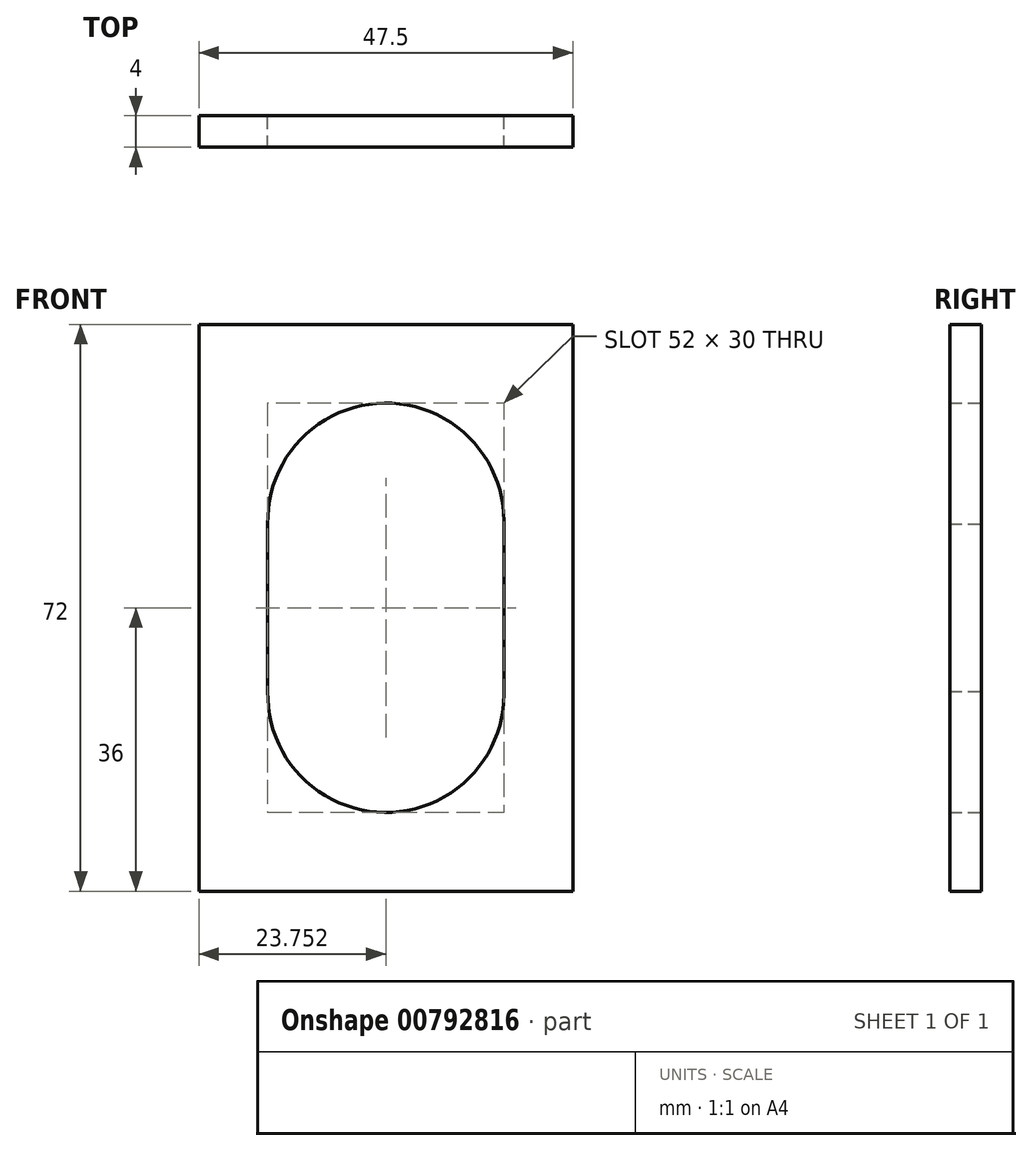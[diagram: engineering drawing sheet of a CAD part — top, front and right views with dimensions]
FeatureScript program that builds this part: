
annotation { "Feature Type Name" : "Feature", "Feature Type Description" : "" }
export const myFeature = defineFeature(function(context is Context, id is Id, definition is map)
    precondition{}
    {
        {
            var Q0;
            Q0=qCreatedBy(makeId("Front.planeOp"),FACE);
            var sketch = newSketch(context, id + "F0", { "sketchPlane" : qUnion([Q0])});
            skLineSegment(sketch, "E0.bottom", {"start": v(23.75, 36) * mm, "end": v(-23.75, 36) * mm});
            skLineSegment(sketch, "E0.top", {"start": v(23.75, -36) * mm, "end": v(-23.75, -36) * mm});
            skLineSegment(sketch, "E0.left", {"start": v(23.75, 36) * mm, "end": v(23.75, -36) * mm});
            skLineSegment(sketch, "E0.right", {"start": v(-23.75, 36) * mm, "end": v(-23.75, -36) * mm});
            skPoint(sketch, "E0.middle", {"position": v(0, 0) * mm});
            skCircle(sketch, "E1", {"center": v(0, 11) * mm, "radius": 15 * mm});
            skCircle(sketch, "E2", {"center": v(0, -11) * mm, "radius": 15 * mm});
            skLineSegment(sketch, "E3", {"start": v(-15, 11.37) * mm, "end": v(-15, -11.37) * mm});
            skLineSegment(sketch, "E4", {"start": v(15, 11) * mm, "end": v(15, -11) * mm});
            skSolve(sketch);
        }
        {
            var Q0;
            Q0 = qSketchRegion(id + "F0", true);
            extrude(context, id + "F1", {"entities" : qUnion([Q0]), "depth" : 4 * mm, "offsetDistance" : 25 * mm});
        }
    });
